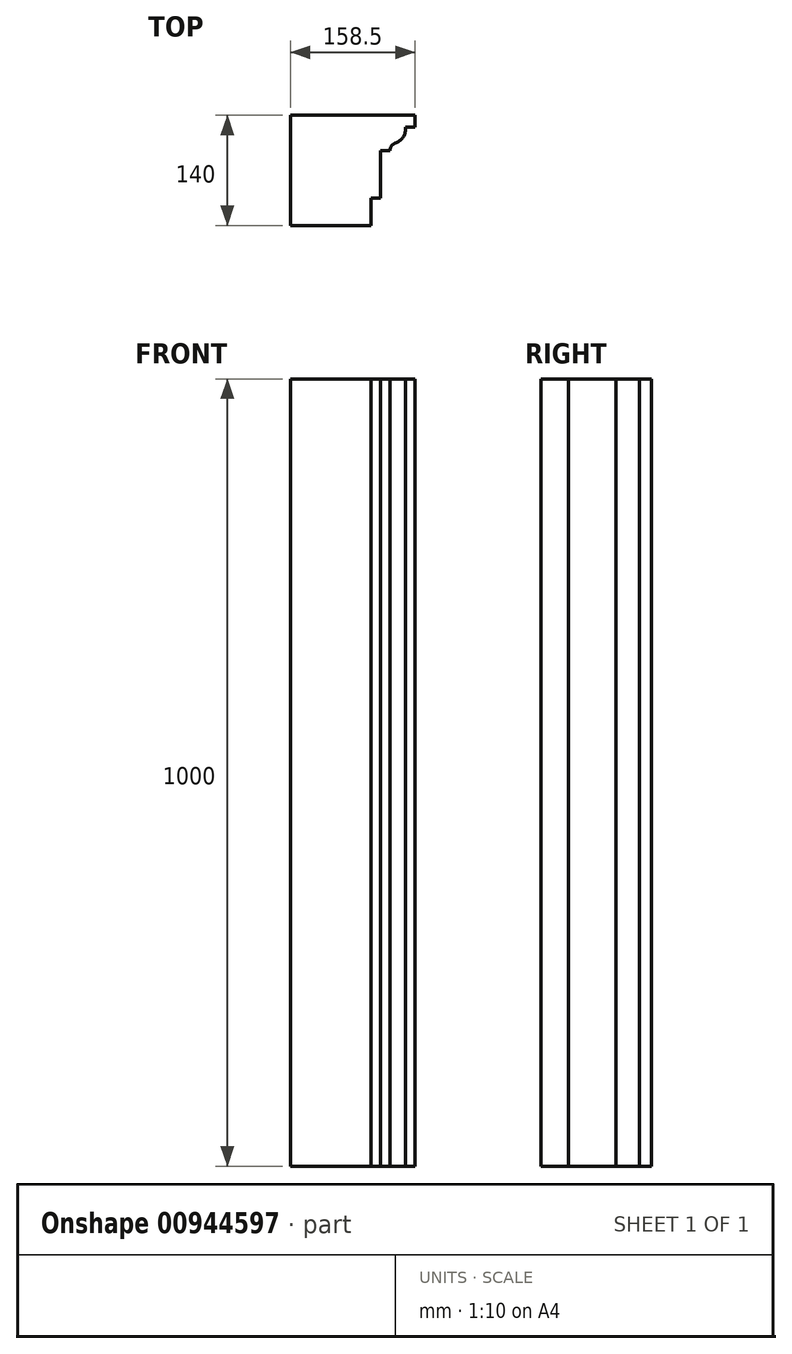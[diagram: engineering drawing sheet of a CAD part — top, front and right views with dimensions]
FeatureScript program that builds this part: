
annotation { "Feature Type Name" : "Feature", "Feature Type Description" : "" }
export const myFeature = defineFeature(function(context is Context, id is Id, definition is map)
    precondition{}
    {
        {
            var Q0;
            Q0=qCreatedBy(makeId("Top.planeOp"),FACE);
            var sketch = newSketch(context, id + "F0", { "sketchPlane" : qUnion([Q0])});
            skLineSegment(sketch, "E0", {"start": v(-87.82, 69.6) * mm, "end": v(-87.82, -70.4) * mm});
            skLineSegment(sketch, "E1", {"start": v(-87.82, -70.4) * mm, "end": v(14.68, -70.4) * mm});
            skLineSegment(sketch, "E2", {"start": v(14.68, -70.4) * mm, "end": v(14.68, -35.4) * mm});
            skLineSegment(sketch, "E3", {"start": v(14.68, -35.4) * mm, "end": v(26.68, -35.4) * mm});
            skLineSegment(sketch, "E4", {"start": v(26.68, -35.4) * mm, "end": v(26.68, 24.6) * mm});
            skLineSegment(sketch, "E5", {"start": v(26.68, 24.6) * mm, "end": v(38.68, 24.6) * mm});
            skArc(sketch, "E6", {"start": v(45.37, 34.04) * mm, "mid": v(40.52, 30.39) * mm, "end": v(38.68, 24.6) * mm});
            skArc(sketch, "E7", {"start": v(45.37, 34.04) * mm, "mid": v(55.54, 42.05) * mm, "end": v(58.68, 54.6) * mm});
            skLineSegment(sketch, "E8", {"start": v(38.68, 24.6) * mm, "end": v(48.68, 24.6) * mm, "construction": true});
            skLineSegment(sketch, "E9", {"start": v(58.68, 54.6) * mm, "end": v(70.68, 54.6) * mm});
            skLineSegment(sketch, "E10", {"start": v(70.68, 54.6) * mm, "end": v(70.68, 69.6) * mm});
            skLineSegment(sketch, "E11", {"start": v(-87.82, 69.6) * mm, "end": v(70.68, 69.6) * mm});
            skSolve(sketch);
        }
        {
            var Q0;
            Q0 = qSketchRegion(id + "F0", true);
            extrude(context, id + "F1", {"entities" : qUnion([Q0]), "depth" : 1000 * mm, "offsetDistance" : 25 * mm});
        }
    });
